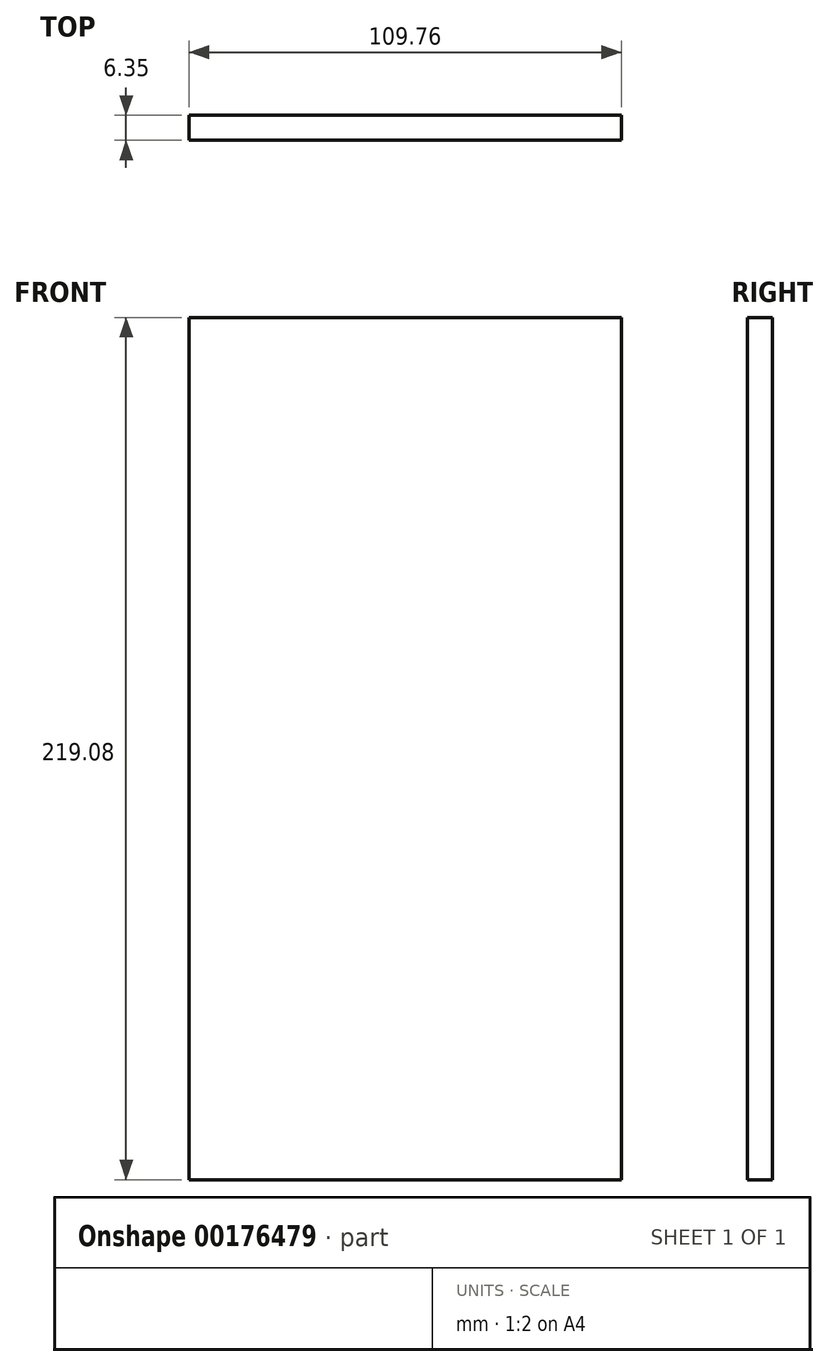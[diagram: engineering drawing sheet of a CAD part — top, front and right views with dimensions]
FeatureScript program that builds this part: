
annotation { "Feature Type Name" : "Feature", "Feature Type Description" : "" }
export const myFeature = defineFeature(function(context is Context, id is Id, definition is map)
    precondition{}
    {
        {
            var Q0;
            Q0=qCreatedBy(makeId("Front.planeOp"),FACE);
            var sketch = newSketch(context, id + "F0", { "sketchPlane" : qUnion([Q0])});
            skLineSegment(sketch, "E0.bottom", {"start": v(-62.1, -88.05) * mm, "end": v(47.66, -88.05) * mm});
            skLineSegment(sketch, "E0.top", {"start": v(-62.1, 131.03) * mm, "end": v(47.66, 131.03) * mm});
            skLineSegment(sketch, "E0.left", {"start": v(-62.1, -88.05) * mm, "end": v(-62.1, 131.03) * mm});
            skLineSegment(sketch, "E0.right", {"start": v(47.66, -88.05) * mm, "end": v(47.66, 131.03) * mm});
            skSolve(sketch);
        }
        {
            var Q0;
            Q0=makeQuery(id+"F0.imprint","IMPRINT",FACE,{"disambiguationData":[TD([[makeQuery(id+"F0.imprint","IMPRINT",EDGE,{"derivedFrom":sQuery(id+"F0.wireOp",EDGE,"E0.bottom")}),1.0]])]});
            extrude(context, id + "F1", {"entities" : qUnion([Q0]), "depth" : 6.35 * mm});
        }
    });
